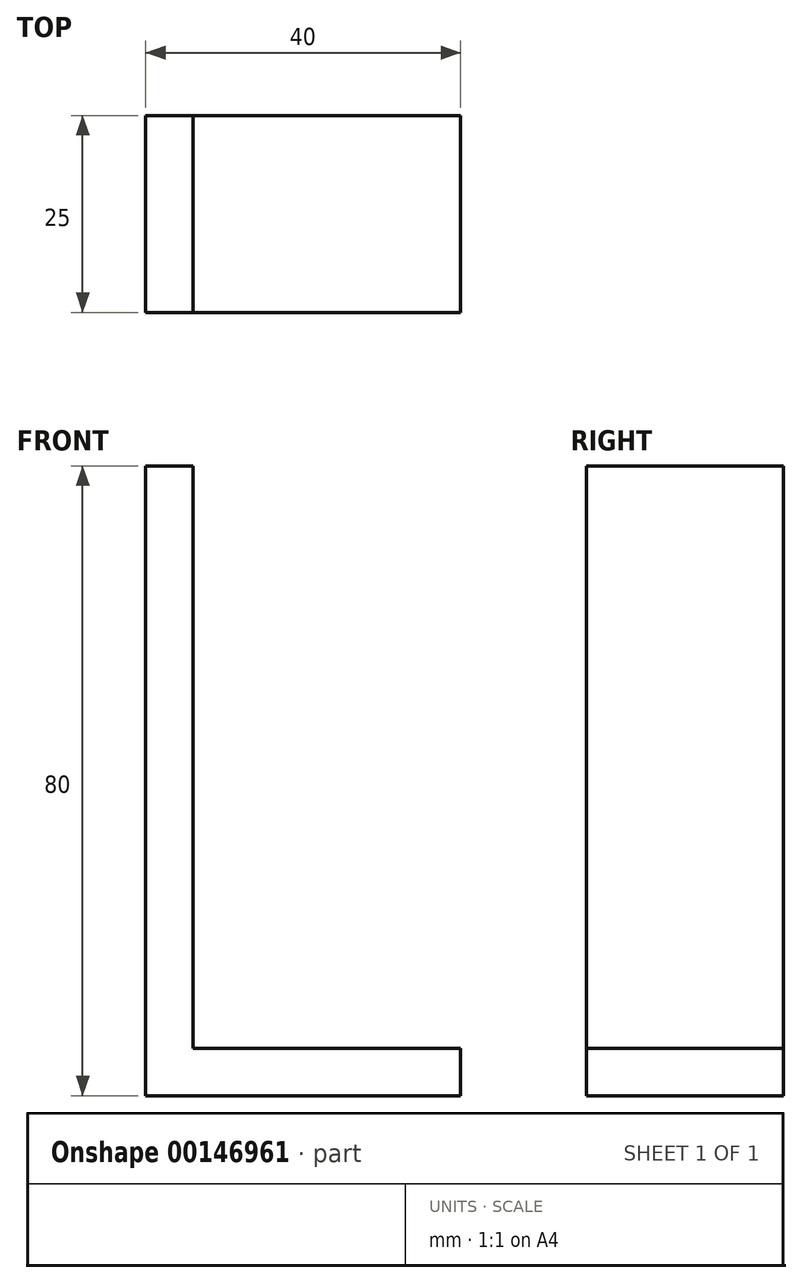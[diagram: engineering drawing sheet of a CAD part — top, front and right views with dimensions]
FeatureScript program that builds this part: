
annotation { "Feature Type Name" : "Feature", "Feature Type Description" : "" }
export const myFeature = defineFeature(function(context is Context, id is Id, definition is map)
    precondition{}
    {
        {
            var Q0;
            Q0=qCreatedBy(makeId("Front.planeOp"),FACE);
            var sketch = newSketch(context, id + "F0", { "sketchPlane" : qUnion([Q0])});
            skLineSegment(sketch, "E0.bottom", {"start": v(0, 0) * mm, "end": v(6, 0) * mm});
            skLineSegment(sketch, "E0.top", {"start": v(0, 80) * mm, "end": v(6, 80) * mm});
            skLineSegment(sketch, "E0.left", {"start": v(0, 0) * mm, "end": v(0, 80) * mm});
            skLineSegment(sketch, "E0.right", {"start": v(6, 0) * mm, "end": v(6, 80) * mm});
            skLineSegment(sketch, "E1.bottom", {"start": v(6, 0) * mm, "end": v(40, 0) * mm});
            skLineSegment(sketch, "E1.top", {"start": v(6, 6) * mm, "end": v(40, 6) * mm});
            skLineSegment(sketch, "E1.left", {"start": v(6, 0) * mm, "end": v(6, 6) * mm});
            skLineSegment(sketch, "E1.right", {"start": v(40, 0) * mm, "end": v(40, 6) * mm});
            skSolve(sketch);
        }
        {
            var Q0;
            Q0 = qSketchRegion(id + "F0", true);
            extrude(context, id + "F1", {"entities" : qUnion([Q0]), "depth" : 25 * mm});
        }
    });
